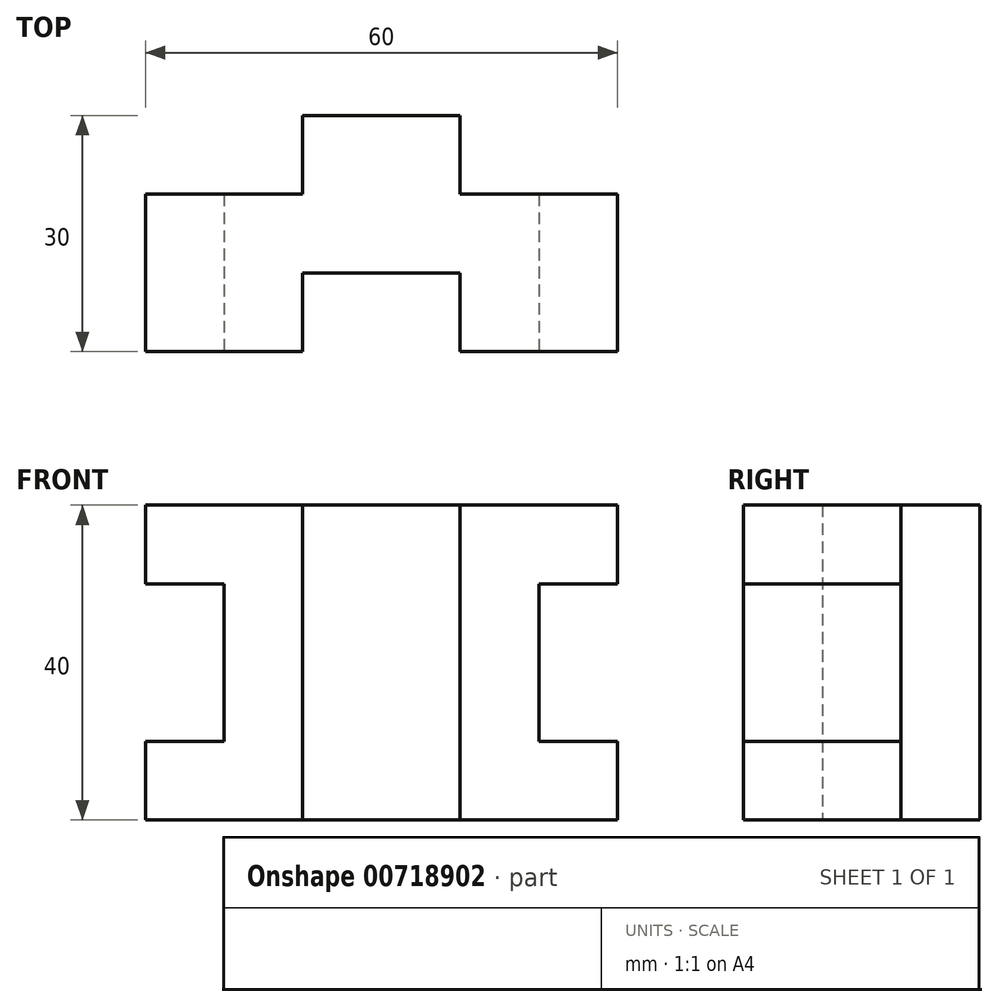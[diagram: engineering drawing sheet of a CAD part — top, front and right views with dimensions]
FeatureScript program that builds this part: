
annotation { "Feature Type Name" : "Feature", "Feature Type Description" : "" }
export const myFeature = defineFeature(function(context is Context, id is Id, definition is map)
    precondition{}
    {
        {
            var Q0;
            Q0=qCreatedBy(makeId("Top.planeOp"),FACE);
            var sketch = newSketch(context, id + "F0", { "sketchPlane" : qUnion([Q0])});
            skLineSegment(sketch, "E0.bottom", {"start": v(30, 10) * mm, "end": v(-30, 10) * mm});
            skLineSegment(sketch, "E0.top", {"start": v(30, -10) * mm, "end": v(-30, -10) * mm});
            skLineSegment(sketch, "E0.left", {"start": v(30, 10) * mm, "end": v(30, -10) * mm});
            skLineSegment(sketch, "E0.right", {"start": v(-30, 10) * mm, "end": v(-30, -10) * mm});
            skLineSegment(sketch, "E1", {"start": v(-10, -10) * mm, "end": v(-10, 0) * mm});
            skLineSegment(sketch, "E2", {"start": v(-10, 0) * mm, "end": v(10, 0) * mm});
            skLineSegment(sketch, "E3", {"start": v(10, 0) * mm, "end": v(10, -10) * mm});
            skLineSegment(sketch, "E4", {"start": v(-10, 10) * mm, "end": v(-10, 20) * mm});
            skLineSegment(sketch, "E5", {"start": v(-10, 20) * mm, "end": v(10, 20) * mm});
            skLineSegment(sketch, "E6", {"start": v(10, 20) * mm, "end": v(10, 10) * mm});
            skSolve(sketch);
        }
        {
            var Q0;
            Q0=makeQuery(id+"F0.imprint","IMPRINT",FACE,{"disambiguationData":[TD([[makeQuery(id+"F0.imprint","IMPRINT",EDGE,{"derivedFrom":sQuery(id+"F0.wireOp",EDGE,"E0.bottom")}),1.0]])]});
            extrude(context, id + "F1", {"entities" : qUnion([Q0]), "depth" : 40 * mm, "offsetDistance" : 25 * mm});
        }
        {
            var Q0;
            {var subQ0=sQuery(id+"F0.wireOp",EDGE,"E4");Q0=makeQuery(id+"F0.imprint","IMPRINT",FACE,{"disambiguationData":[TD([[makeQuery(id+"F0.imprint","IMPRINT",EDGE,{"derivedFrom":subQ0}),-1.0]])]});}
            extrude(context, id + "F2", {"entities" : qUnion([Q0]), "operationType" : NewBodyOperationType.ADD, "depth" : 40 * mm, "offsetDistance" : 25 * mm});
        }
        {
            var Q0;
            {var subQ0=sQuery(id+"F0.wireOp",EDGE,"E0.top");Q0=makeQuery(id+"F1.opExtrude","SWEPT_FACE",FACE,{"disambiguationData":[OSD([subQ0]),TDD([makeQuery(id+"F0.imprint","IMPRINT",EDGE,{"disambiguationData":[TD([[makeQuery(id+"F0.imprint","INTERSECT",VERTEX,{"derivedFrom":[subQ0,sQuery(id+"F0.wireOp",EDGE,"E0.left")]}),-1.0]])],"derivedFrom":subQ0})])]});}
            var sketch = newSketch(context, id + "F3", { "sketchPlane" : qUnion([Q0])});
            skLineSegment(sketch, "E7.bottom", {"start": v(30, 10) * mm, "end": v(20, 10) * mm});
            skLineSegment(sketch, "E7.top", {"start": v(30, 30) * mm, "end": v(20, 30) * mm});
            skLineSegment(sketch, "E7.left", {"start": v(30, 10) * mm, "end": v(30, 30) * mm});
            skLineSegment(sketch, "E7.right", {"start": v(20, 10) * mm, "end": v(20, 30) * mm});
            skLineSegment(sketch, "E8.MirrorCS", {"start": v(-30, 30) * mm, "end": v(-20, 30) * mm});
            skLineSegment(sketch, "E9.MirrorCS", {"start": v(-20, 10) * mm, "end": v(-20, 30) * mm});
            skLineSegment(sketch, "E10.MirrorCS", {"start": v(-30, 10) * mm, "end": v(-20, 10) * mm});
            skLineSegment(sketch, "E11.MirrorCS", {"start": v(-30, 10) * mm, "end": v(-30, 30) * mm});
            skSolve(sketch);
        }
        {
            var Q0;
            Q0=makeQuery(id+"F3.imprint","IMPRINT",FACE,{"disambiguationData":[TD([[makeQuery(id+"F3.imprint","IMPRINT",EDGE,{"derivedFrom":sQuery(id+"F3.wireOp",EDGE,"E7.bottom")}),-1.0]])]});
            var Q1;
            Q1=makeQuery(id+"F3.imprint","IMPRINT",FACE,{"disambiguationData":[TD([[makeQuery(id+"F3.imprint","IMPRINT",EDGE,{"derivedFrom":sQuery(id+"F3.wireOp",EDGE,"E8.MirrorCS")}),-1.0]])]});
            extrude(context, id + "F4", {"entities" : qUnion([Q0, Q1]), "operationType" : NewBodyOperationType.REMOVE, "oppositeDirection" : true, "depth" : 25 * mm, "offsetDistance" : 25 * mm});
        }
    });
